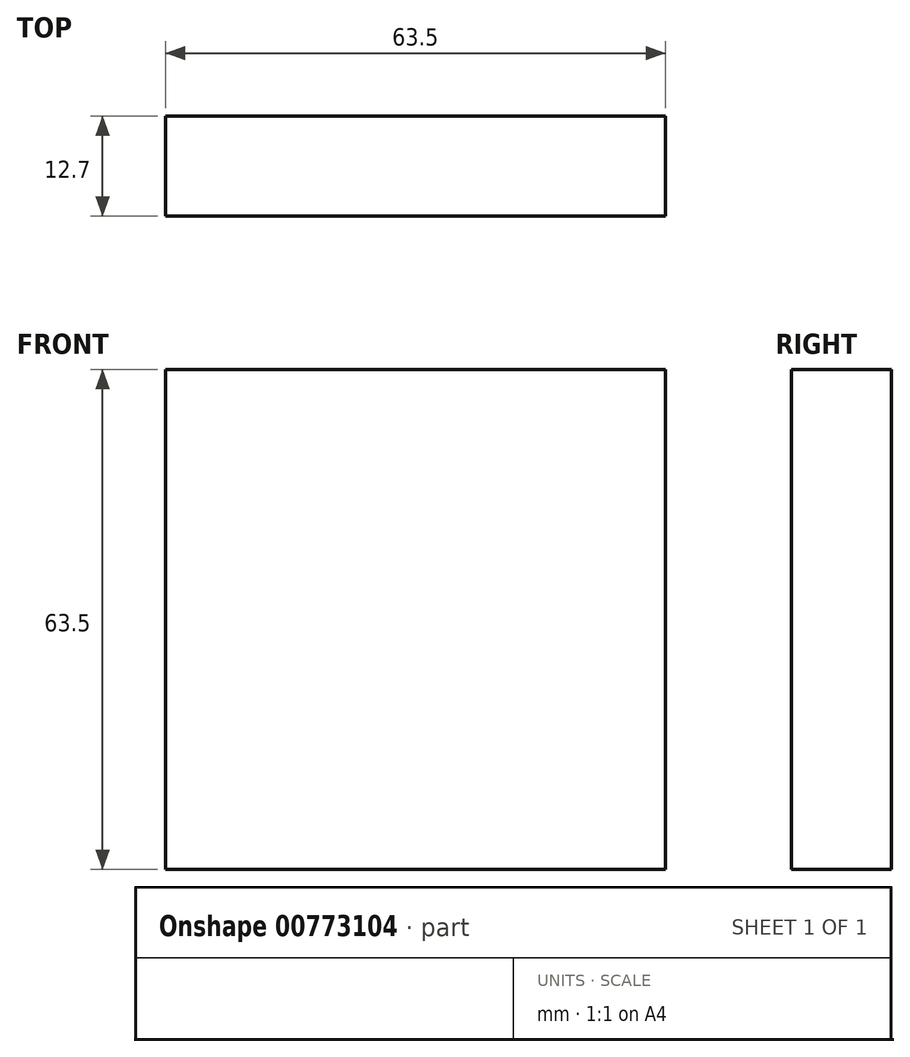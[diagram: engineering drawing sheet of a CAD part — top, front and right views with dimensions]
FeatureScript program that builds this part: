
annotation { "Feature Type Name" : "Feature", "Feature Type Description" : "" }
export const myFeature = defineFeature(function(context is Context, id is Id, definition is map)
    precondition{}
    {
        {
            var Q0;
            Q0=qCreatedBy(makeId("Front.planeOp"),FACE);
            var sketch = newSketch(context, id + "F0", { "sketchPlane" : qUnion([Q0])});
            skLineSegment(sketch, "E0.bottom", {"start": v(0, 63.5) * mm, "end": v(63.5, 63.5) * mm});
            skLineSegment(sketch, "E0.top", {"start": v(0, 0) * mm, "end": v(63.5, 0) * mm});
            skLineSegment(sketch, "E0.left", {"start": v(0, 63.5) * mm, "end": v(0, 0) * mm});
            skLineSegment(sketch, "E0.right", {"start": v(63.5, 63.5) * mm, "end": v(63.5, 0) * mm});
            skSolve(sketch);
        }
        {
            var Q0;
            Q0 = qSketchRegion(id + "F0", true);
            extrude(context, id + "F1", {"entities" : qUnion([Q0]), "depth" : 12.7 * mm, "offsetDistance" : 25.4 * mm});
        }
    });
